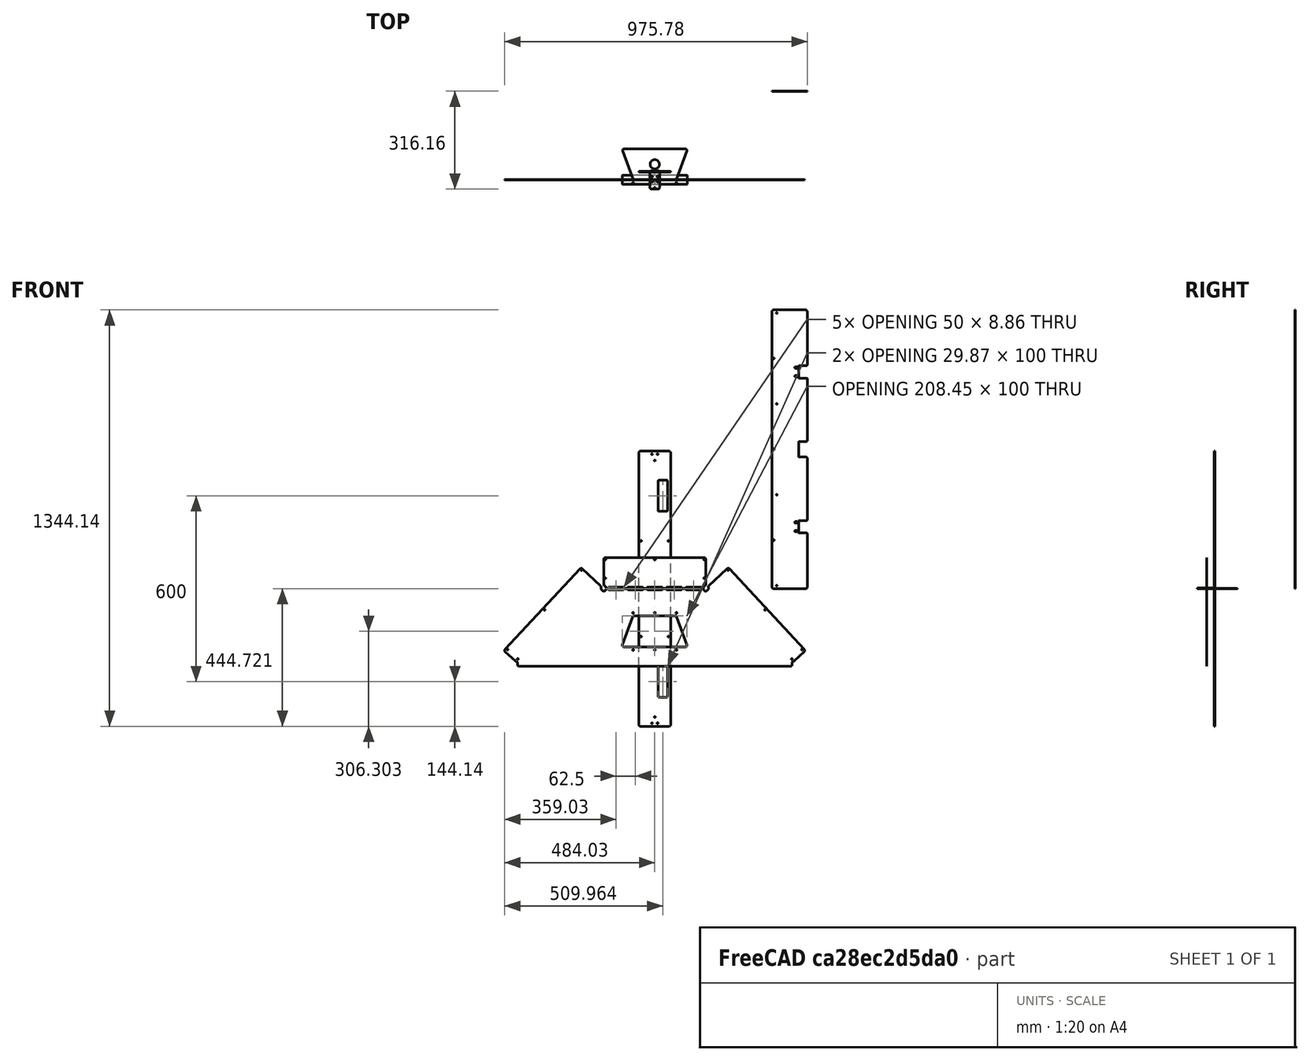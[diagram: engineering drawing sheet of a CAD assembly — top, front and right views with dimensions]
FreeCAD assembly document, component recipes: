
FREECAD ASSEMBLY — COMPONENT RECIPES ("composit_stand12_ss")

This assembly document has 5 components, labeled P0..P4 below (a component is one placed body or linked part). 0 of them carry a construction recipe — the FreeCAD feature program that regenerates the part from scratch, quoted from this document or its linked companion documents; the rest are supplied as boundary geometry only. No exploded tour is included for this assembly.
COMPONENT P0 — geometry summary ("sink_cutout"; no construction recipe available for this part):
  bounding box: 207.5 x 99.0 x 1.5 mm
  tessellated surface: 800 triangles
  volume: 24943 mm^3 (81% of its bounding box)
  symmetry: 2-fold rotationally symmetric about the y axis; mirror-symmetric across its x mid-plane, z mid-plane
COMPONENT P1 — geometry summary ("bar_fix"; no construction recipe available for this part):
  bounding box: 34.0 x 31.0 x 29.0 mm
  tessellated surface: 1,040 triangles
  volume: 3550 mm^3 (12% of its bounding box)
  symmetry: mirror-symmetric across its x mid-plane
COMPONENT P2 — geometry summary ("sink"; no construction recipe available for this part):
  bounding box: 892.7 x 240.0 x 99.5 mm
  tessellated surface: 5,476 triangles
  volume: 112891 mm^3 (1% of its bounding box)
  symmetry: mirror-symmetric across its x mid-plane
COMPONENT P3 — geometry summary ("bar"; no construction recipe available for this part):
  bounding box: 888.3 x 65.0 x 27.0 mm
  tessellated surface: 2,788 triangles
  volume: 182420 mm^3 (12% of its bounding box)
  symmetry: mirror-symmetric across its z mid-plane
COMPONENT P4 — geometry summary ("sink_jumb"; no construction recipe available for this part):
  bounding box: 210.0 x 30.0 x 0.7 mm
  tessellated surface: 452 triangles
  volume: 4389 mm^3 (100% of its bounding box)
  symmetry: 2-fold rotationally symmetric about the x axis; 2-fold rotationally symmetric about the y axis; 2-fold rotationally symmetric about the z axis; mirror-symmetric across its x mid-plane, y mid-plane, z mid-plane
PROVENANCE & LICENSES
A FreeCAD (.FCStd) document from a public repository crawl; recipes are the document's own serialized feature recipes (and, for linked parts, companion documents' recipes).
License: as declared in the source repository (recorded in the dataset sidecar).
